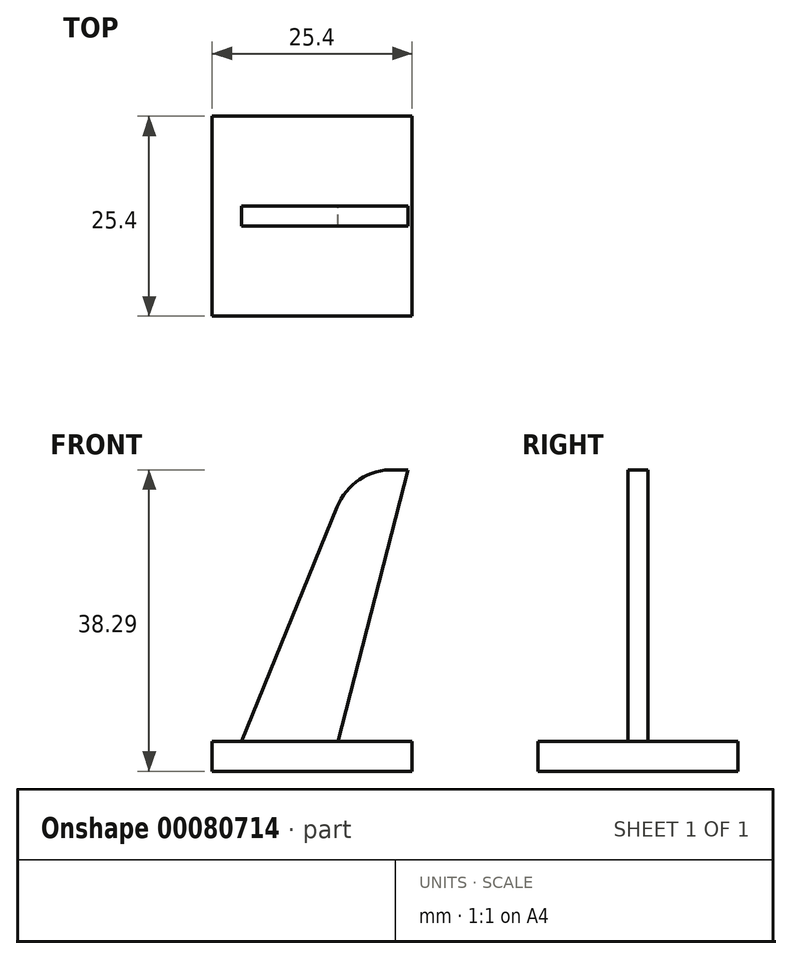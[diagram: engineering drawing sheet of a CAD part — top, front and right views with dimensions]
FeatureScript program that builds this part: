
annotation { "Feature Type Name" : "Feature", "Feature Type Description" : "" }
export const myFeature = defineFeature(function(context is Context, id is Id, definition is map)
    precondition{}
    {
        {
            var Q0;
            Q0=qCreatedBy(makeId("Front.planeOp"),FACE);
            var sketch = newSketch(context, id + "F0", { "sketchPlane" : qUnion([Q0])});
            skLineSegment(sketch, "E0.bottom", {"start": v(-49.84, 1.84) * mm, "end": v(-24.44, 1.84) * mm});
            skLineSegment(sketch, "E0.top", {"start": v(-49.84, -1.97) * mm, "end": v(-24.44, -1.97) * mm});
            skLineSegment(sketch, "E0.left", {"start": v(-49.84, 1.84) * mm, "end": v(-49.84, -1.97) * mm});
            skLineSegment(sketch, "E0.right", {"start": v(-24.44, 1.84) * mm, "end": v(-24.44, -1.97) * mm});
            skLineSegment(sketch, "E1", {"start": v(-37.14, 1.84) * mm, "end": v(-37.14, -1.97) * mm, "construction": true});
            skLineSegment(sketch, "E2", {"start": v(-46.14, 1.84) * mm, "end": v(-32, 36.48) * mm});
            skLineSegment(sketch, "E3", {"start": v(-32, 36.48) * mm, "end": v(-24.97, 36.27) * mm});
            skLineSegment(sketch, "E4", {"start": v(-24.97, 36.27) * mm, "end": v(-33.86, 1.84) * mm});
            skSolve(sketch);
        }
        {
            var Q0;
            {var subQ0=sQuery(id+"F0.wireOp",EDGE,"E0.left");Q0=makeQuery(id+"F0.imprint","IMPRINT",FACE,{"disambiguationData":[TD([[makeQuery(id+"F0.imprint","IMPRINT",EDGE,{"derivedFrom":subQ0}),1.0]])]});}
            var Q1;
            {var subQ0=sQuery(id+"F0.wireOp",EDGE,"E0.right");Q1=makeQuery(id+"F0.imprint","IMPRINT",FACE,{"disambiguationData":[TD([[makeQuery(id+"F0.imprint","IMPRINT",EDGE,{"derivedFrom":subQ0}),-1.0]])]});}
            var Q2;
            {var subQ0=sQuery(id+"F0.wireOp",EDGE,"Ilnx5Fgz-1rpX-weBC-XK9i-kBVCUjVR36G6");var subQ1=sQuery(id+"F0.wireOp",EDGE,"E0.bottom");var subQ2=makeQuery(id+"F0.imprint","INTERSECT",VERTEX,{"derivedFrom":[subQ1,subQ0]});Q2=makeQuery(id+"F0.imprint","IMPRINT",FACE,{"disambiguationData":[TD([[makeQuery(id+"F0.imprint","IMPRINT",EDGE,{"disambiguationData":[TD([[subQ2,-1.0]])],"derivedFrom":subQ1}),-1.0]])]});}
            extrude(context, id + "F1", {"entities" : qUnion([Q0, Q1, Q2]), "endBound" : BoundingType.SYMMETRIC, "depth" : 25.4 * mm});
        }
        {
            var Q0;
            {var subQ5=sQuery(id+"F0.wireOp",EDGE,"iRgmnSOd-ucyk-gQYY-P5Rp-kRFYHJy7zjb5");Q0=makeQuery(id+"F0.imprint","IMPRINT",FACE,{"disambiguationData":[TD([[makeQuery(id+"F0.imprint","IMPRINT",EDGE,{"derivedFrom":subQ5}),-1.0]])]});}
            var Q1;
            {var subQ0=sQuery(id+"F0.wireOp",EDGE,"E2");Q1=makeQuery(id+"F0.imprint","IMPRINT",FACE,{"disambiguationData":[TD([[makeQuery(id+"F0.imprint","IMPRINT",EDGE,{"derivedFrom":subQ0}),-1.0]])]});}
            extrude(context, id + "F2", {"entities" : qUnion([Q0, Q1]), "operationType" : NewBodyOperationType.ADD, "endBound" : BoundingType.SYMMETRIC, "depth" : 2.54 * mm});
        }
        {
            var Q0;
            Q0=makeQuery(id+"F2.opExtrude","SWEPT_EDGE",EDGE,{"disambiguationData":[OSD([sQuery(id+"F0.wireOp",EDGE,"E2"),sQuery(id+"F0.wireOp",EDGE,"E3")])]});
            fillet(context, id + "F3", {"entities" : qUnion([Q0]), "radius" : 7.62 * mm, "tangentPropagation" : true, "allowEdgeOverflow" : false});
        }
    });
